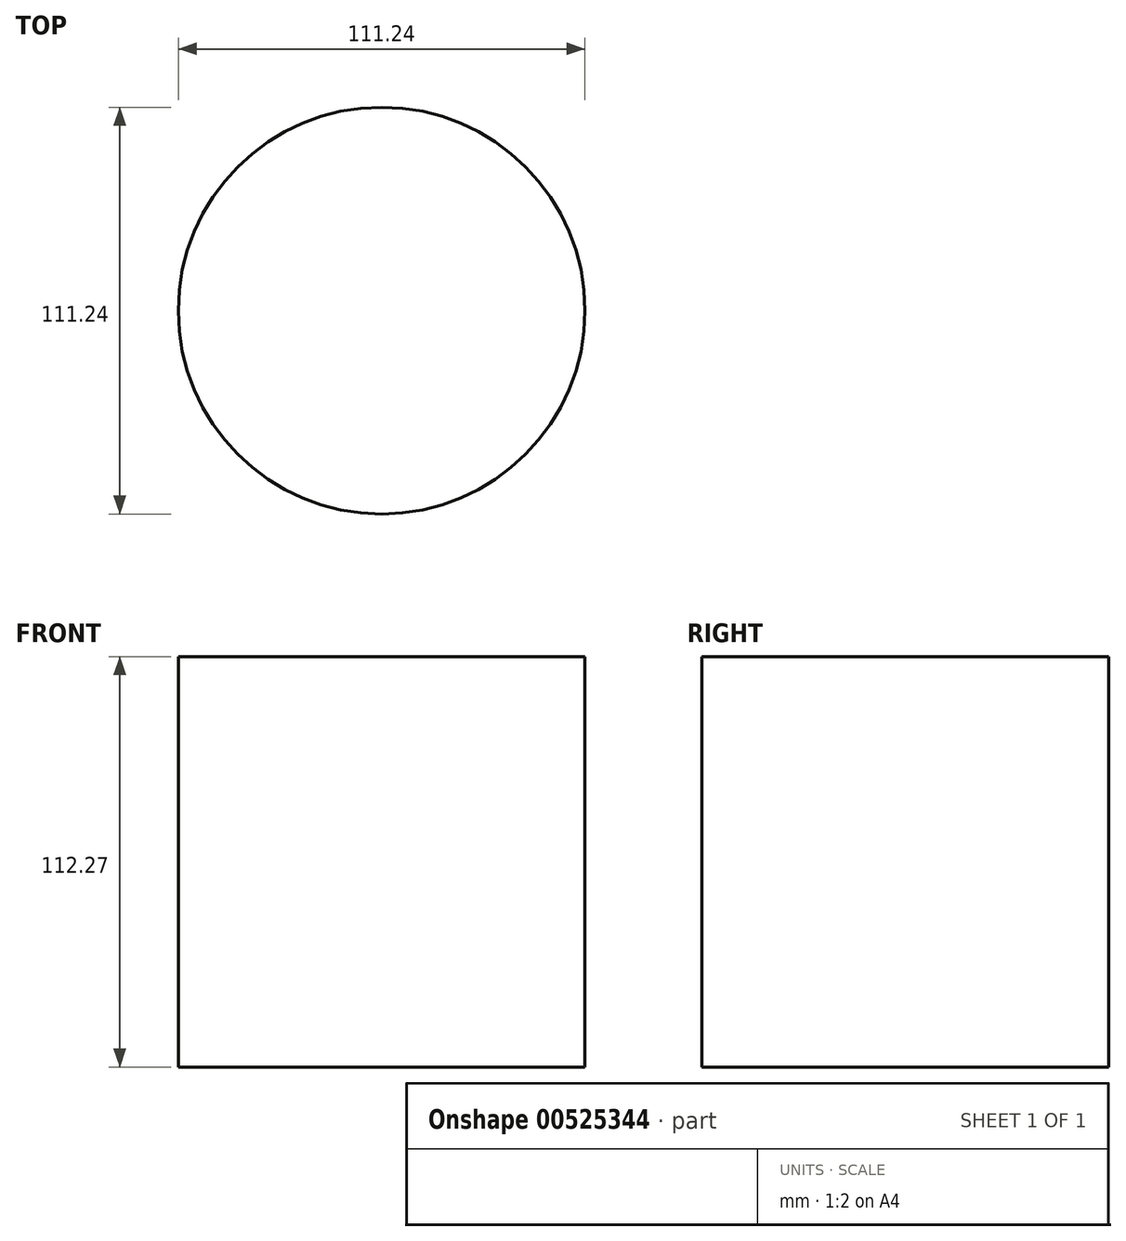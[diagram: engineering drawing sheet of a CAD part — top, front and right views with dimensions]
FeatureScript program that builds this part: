
annotation { "Feature Type Name" : "Feature", "Feature Type Description" : "" }
export const myFeature = defineFeature(function(context is Context, id is Id, definition is map)
    precondition{}
    {
        {
            var Q0;
            Q0=qCreatedBy(makeId("Top.planeOp"),FACE);
            var sketch = newSketch(context, id + "F0", { "sketchPlane" : qUnion([Q0])});
            skCircle(sketch, "E0", {"center": v(0, 0) * mm, "radius": 55.62 * mm});
            skSolve(sketch);
        }
        {
            var Q0;
            Q0=makeQuery(id+"F0.imprint","IMPRINT",FACE,{"disambiguationData":[TD([[makeQuery(id+"F0.imprint","IMPRINT",EDGE,{"derivedFrom":sQuery(id+"F0.wireOp",EDGE,"E0")}),1.0]])]});
            extrude(context, id + "F1", {"entities" : qUnion([Q0]), "depth" : 112.27 * mm, "offsetDistance" : 25.4 * mm});
        }
    });
